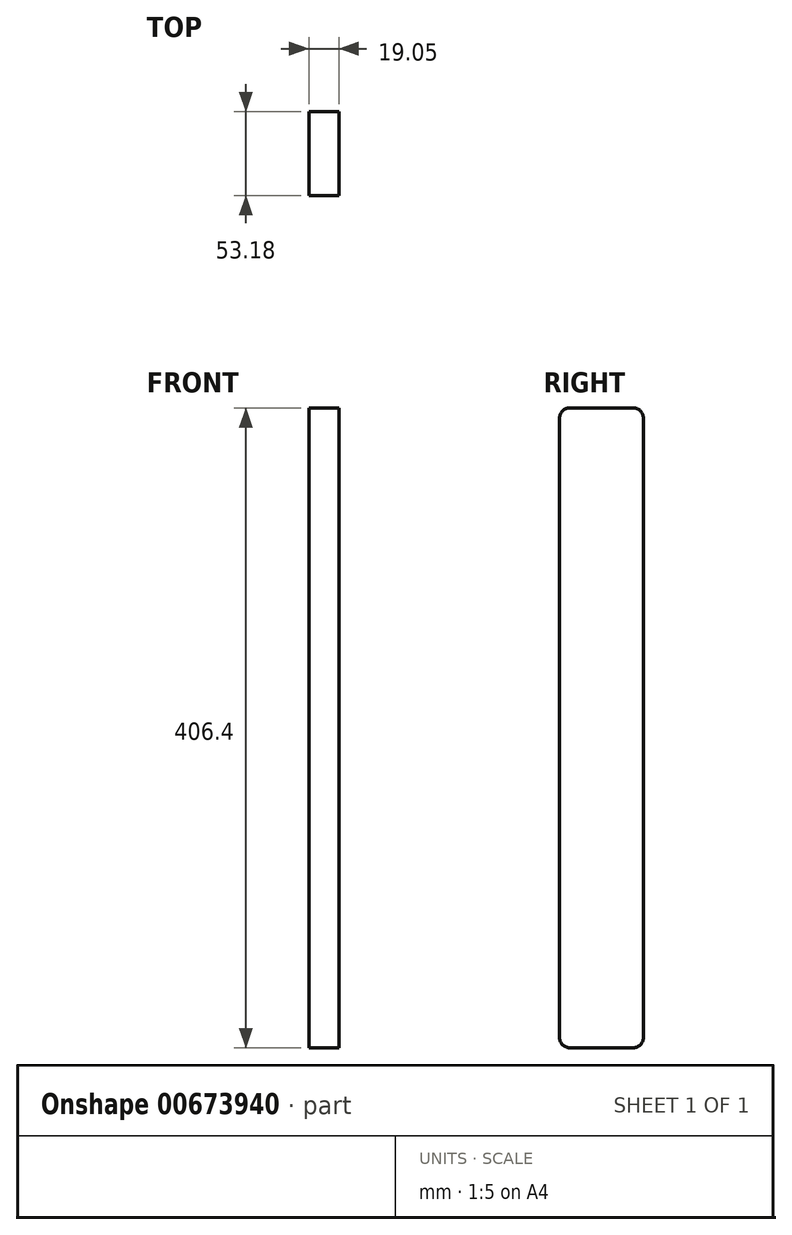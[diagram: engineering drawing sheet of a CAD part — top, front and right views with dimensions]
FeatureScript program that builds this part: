
annotation { "Feature Type Name" : "Feature", "Feature Type Description" : "" }
export const myFeature = defineFeature(function(context is Context, id is Id, definition is map)
    precondition{}
    {
        {
            var Q0;
            Q0=qCreatedBy(makeId("Right.planeOp"),FACE);
            var sketch = newSketch(context, id + "F0", { "sketchPlane" : qUnion([Q0])});
            skLineSegment(sketch, "E0.bottom", {"start": v(-68.8, 209.34) * mm, "end": v(-28.31, 209.34) * mm});
            skLineSegment(sketch, "E0.top", {"start": v(-68.8, -197.06) * mm, "end": v(-28.31, -197.06) * mm});
            skLineSegment(sketch, "E0.left", {"start": v(-75.14, 203) * mm, "end": v(-75.14, -190.7) * mm});
            skLineSegment(sketch, "E0.right", {"start": v(-21.96, 203) * mm, "end": v(-21.96, -190.7) * mm});
            skPoint(sketch, "E1.visualSharp", {"position": v(-75.14, 209.34) * mm});
            skArc(sketch, "E1.filletArc", {"start": v(-68.8, 209.34) * mm, "mid": v(-73.28, 207.48) * mm, "end": v(-75.14, 203) * mm});
            skPoint(sketch, "E2.visualSharp", {"position": v(-75.14, -197.06) * mm});
            skArc(sketch, "E2.filletArc", {"start": v(-75.14, -190.7) * mm, "mid": v(-73.28, -195.2) * mm, "end": v(-68.8, -197.06) * mm});
            skPoint(sketch, "E3.visualSharp", {"position": v(-21.96, -197.06) * mm});
            skArc(sketch, "E3.filletArc", {"start": v(-28.31, -197.06) * mm, "mid": v(-23.82, -195.2) * mm, "end": v(-21.96, -190.7) * mm});
            skPoint(sketch, "E4.visualSharp", {"position": v(-21.96, 209.34) * mm});
            skArc(sketch, "E4.filletArc", {"start": v(-21.96, 203) * mm, "mid": v(-23.82, 207.48) * mm, "end": v(-28.31, 209.34) * mm});
            skSolve(sketch);
        }
        {
            var Q0;
            Q0=makeQuery(id+"F0.imprint","IMPRINT",FACE,{"disambiguationData":[TD([[makeQuery(id+"F0.imprint","IMPRINT",EDGE,{"derivedFrom":sQuery(id+"F0.wireOp",EDGE,"E0.bottom")}),-1.0]])]});
            extrude(context, id + "F1", {"entities" : qUnion([Q0]), "depth" : 19.05 * mm, "offsetDistance" : 25.4 * mm});
        }
    });
